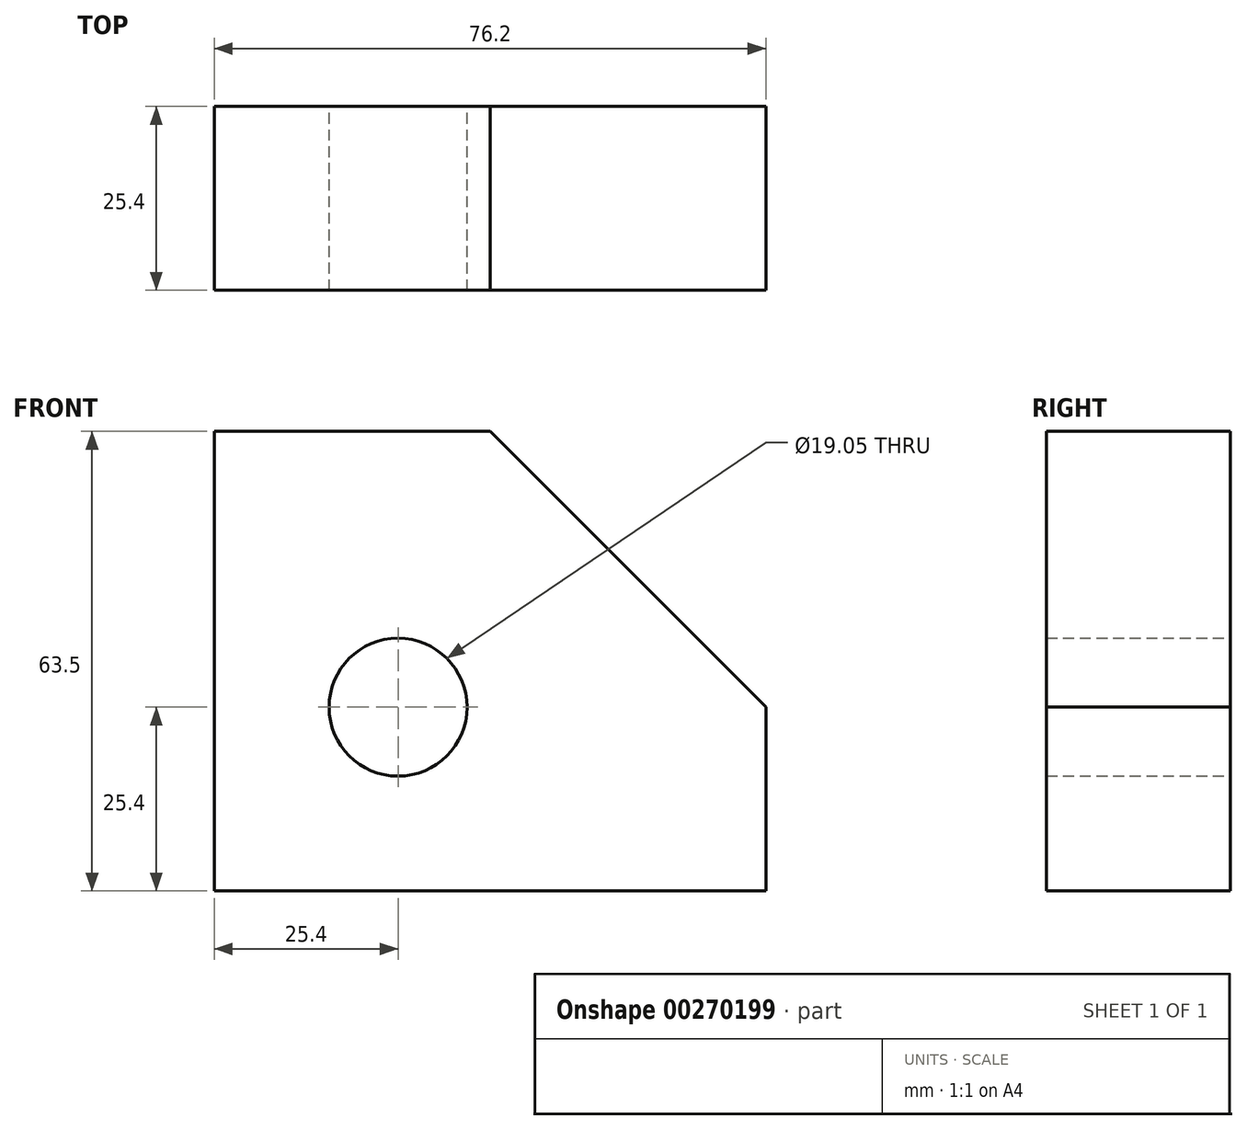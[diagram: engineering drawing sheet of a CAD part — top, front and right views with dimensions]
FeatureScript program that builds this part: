
annotation { "Feature Type Name" : "Feature", "Feature Type Description" : "" }
export const myFeature = defineFeature(function(context is Context, id is Id, definition is map)
    precondition{}
    {
        {
            var Q0;
            Q0=qCreatedBy(makeId("Front.planeOp"),FACE);
            var sketch = newSketch(context, id + "F0", { "sketchPlane" : qUnion([Q0])});
            skLineSegment(sketch, "E0", {"start": v(76.2, 0) * mm, "end": v(76.2, 25.4) * mm});
            skLineSegment(sketch, "E1", {"start": v(38.1, 63.5) * mm, "end": v(76.2, 25.4) * mm});
            skLineSegment(sketch, "E2", {"start": v(38.1, 63.5) * mm, "end": v(0, 63.5) * mm});
            skLineSegment(sketch, "E3", {"start": v(0, 0) * mm, "end": v(76.2, 0) * mm});
            skLineSegment(sketch, "E4", {"start": v(0, 63.5) * mm, "end": v(0, 0) * mm});
            skCircle(sketch, "E5", {"center": v(25.4, 25.4) * mm, "radius": 9.53 * mm});
            skPoint(sketch, "E5.centerSnap0", {"position": v(0, 25.4) * mm});
            skSolve(sketch);
        }
        {
            var Q0;
            Q0=qSketchRegion(id+"F0",true);
            extrude(context, id + "F1", {"entities" : qUnion([Q0]), "depth" : 25.4 * mm, "symmetric" : true});
        }
    });
